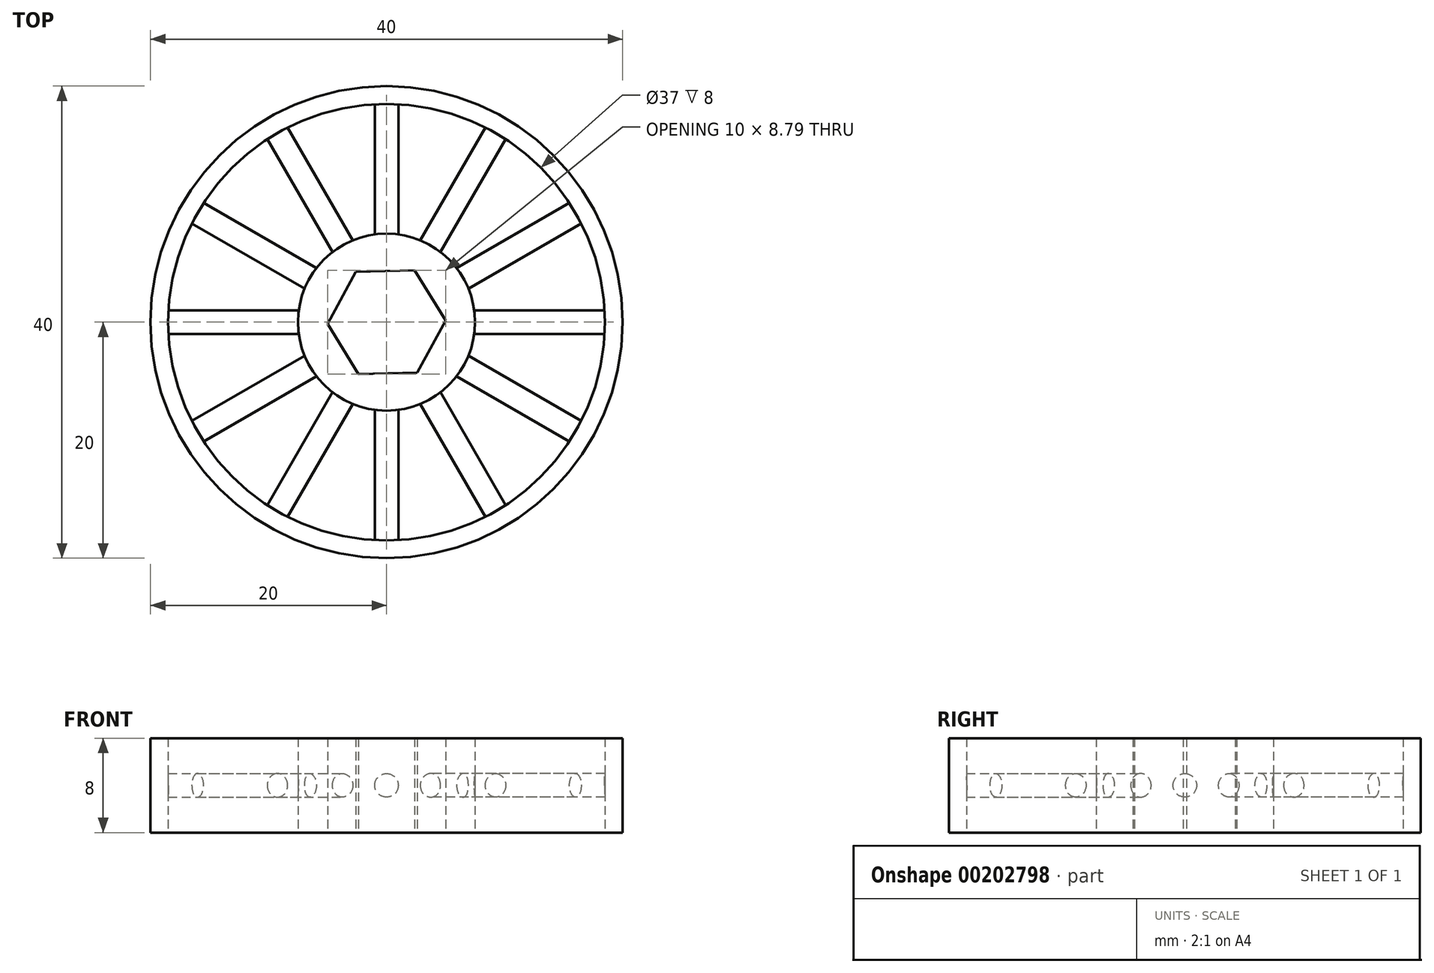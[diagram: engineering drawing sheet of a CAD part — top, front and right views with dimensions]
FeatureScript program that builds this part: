
annotation { "Feature Type Name" : "Feature", "Feature Type Description" : "" }
export const myFeature = defineFeature(function(context is Context, id is Id, definition is map)
    precondition{}
    {
        {
            var Q0;
            Q0=qCreatedBy(makeId("Top.planeOp"),FACE);
            var sketch = newSketch(context, id + "F0", { "sketchPlane" : qUnion([Q0])});
            skCircle(sketch, "E0", {"center": v(0, 0) * mm, "radius": 20 * mm});
            skCircle(sketch, "E1", {"center": v(0, 0) * mm, "radius": 5 * mm});
            skCircle(sketch, "E2", {"center": v(0, 0) * mm, "radius": 7.5 * mm});
            skCircle(sketch, "E3.cCircle", {"center": v(0, 0) * mm, "radius": 5 * mm, "construction": true});
            skLineSegment(sketch, "E3.0", {"start": v(2.61, -4.26) * mm, "end": v(-2.39, -4.4) * mm});
            skLineSegment(sketch, "E3.1", {"start": v(-2.39, -4.4) * mm, "end": v(-5, -0.13) * mm});
            skLineSegment(sketch, "E3.2", {"start": v(-5, -0.13) * mm, "end": v(-2.61, 4.26) * mm});
            skLineSegment(sketch, "E3.3", {"start": v(-2.61, 4.26) * mm, "end": v(2.39, 4.4) * mm});
            skLineSegment(sketch, "E3.4", {"start": v(2.39, 4.4) * mm, "end": v(5, 0.13) * mm});
            skLineSegment(sketch, "E3.5", {"start": v(5, 0.13) * mm, "end": v(2.61, -4.26) * mm});
            skCircle(sketch, "E4.0", {"center": v(0, 0) * mm, "radius": 18.5 * mm});
            skLineSegment(sketch, "E5.trimOffspring", {"start": v(7.5, 0) * mm, "end": v(18.5, 0) * mm, "construction": true});
            skLineSegment(sketch, "E6.0", {"start": v(7.43, -1) * mm, "end": v(18.47, -1) * mm});
            skLineSegment(sketch, "E7.0", {"start": v(7.43, 1) * mm, "end": v(18.47, 1) * mm});
            skSolve(sketch);
        }
        {
            var Q0;
            Q0=makeQuery(id+"F0.imprint","IMPRINT",FACE,{"disambiguationData":[TD([[makeQuery(id+"F0.imprint","IMPRINT",EDGE,{"derivedFrom":sQuery(id+"F0.wireOp",EDGE,"E0")}),1.0]])]});
            var Q1;
            Q1=makeQuery(id+"F0.imprint","IMPRINT",FACE,{"disambiguationData":[TD([[makeQuery(id+"F0.imprint","IMPRINT",EDGE,{"derivedFrom":sQuery(id+"F0.wireOp",EDGE,"E2")}),1.0]])]});
            var Q2;
            {var subQ0=sQuery(id+"F0.wireOp",EDGE,"E3.1");Q2=makeQuery(id+"F0.imprint","IMPRINT",FACE,{"disambiguationData":[TD([[makeQuery(id+"F0.imprint","IMPRINT",EDGE,{"derivedFrom":subQ0}),1.0]])]});}
            var Q3;
            {var subQ0=sQuery(id+"F0.wireOp",EDGE,"E3.2");Q3=makeQuery(id+"F0.imprint","IMPRINT",FACE,{"disambiguationData":[TD([[makeQuery(id+"F0.imprint","IMPRINT",EDGE,{"derivedFrom":subQ0}),1.0]])]});}
            var Q4;
            {var subQ0=sQuery(id+"F0.wireOp",EDGE,"E3.3");Q4=makeQuery(id+"F0.imprint","IMPRINT",FACE,{"disambiguationData":[TD([[makeQuery(id+"F0.imprint","IMPRINT",EDGE,{"derivedFrom":subQ0}),1.0]])]});}
            var Q5;
            {var subQ0=sQuery(id+"F0.wireOp",EDGE,"E3.4");Q5=makeQuery(id+"F0.imprint","IMPRINT",FACE,{"disambiguationData":[TD([[makeQuery(id+"F0.imprint","IMPRINT",EDGE,{"derivedFrom":subQ0}),1.0]])]});}
            var Q6;
            {var subQ0=sQuery(id+"F0.wireOp",EDGE,"E3.5");Q6=makeQuery(id+"F0.imprint","IMPRINT",FACE,{"disambiguationData":[TD([[makeQuery(id+"F0.imprint","IMPRINT",EDGE,{"derivedFrom":subQ0}),1.0]])]});}
            var Q7;
            {var subQ0=sQuery(id+"F0.wireOp",EDGE,"E3.0");Q7=makeQuery(id+"F0.imprint","IMPRINT",FACE,{"disambiguationData":[TD([[makeQuery(id+"F0.imprint","IMPRINT",EDGE,{"derivedFrom":subQ0}),1.0]])]});}
            extrude(context, id + "F1", {"entities" : qUnion([Q0, Q1, Q2, Q3, Q4, Q5, Q6, Q7]), "depth" : 4 * mm, "hasSecondDirection" : true, "secondDirectionOppositeDirection" : true, "secondDirectionDepth" : 4 * mm});
        }
        {
            var Q0;
            {var subQ0=sQuery(id+"F0.wireOp",EDGE,"E6.0");Q0=makeQuery(id+"F0.imprint","IMPRINT",FACE,{"disambiguationData":[TD([[makeQuery(id+"F0.imprint","IMPRINT",EDGE,{"derivedFrom":subQ0}),1.0]])]});}
            extrude(context, id + "F2", {"entities" : qUnion([Q0]), "depth" : 1 * mm, "hasSecondDirection" : true, "secondDirectionOppositeDirection" : true, "secondDirectionDepth" : 1 * mm});
        }
        {
            var Q0;
            Q0=qCreatedBy(makeId("Right.planeOp"),FACE);
            var sketch = newSketch(context, id + "F3", { "sketchPlane" : qUnion([Q0])});
            skLineSegment(sketch, "E8", {"start": v(0, -29.36) * mm, "end": v(0, 29.36) * mm, "construction": true});
            skSolve(sketch);
        }
        {
            var Q0;
            Q0=makeQuery(id+"F2.opExtrude","CAP_EDGE",EDGE,{"disambiguationData":[OSD([sQuery(id+"F0.wireOp",EDGE,"E6.0")])],"isStart":false});
            var Q1;
            Q1=makeQuery(id+"F2.opExtrude","CAP_EDGE",EDGE,{"disambiguationData":[OSD([sQuery(id+"F0.wireOp",EDGE,"E7.0")])],"isStart":false});
            var Q2;
            Q2=makeQuery(id+"F2.opExtrude","CAP_EDGE",EDGE,{"disambiguationData":[OSD([sQuery(id+"F0.wireOp",EDGE,"E6.0")])],"isStart":true});
            var Q3;
            Q3=makeQuery(id+"F2.opExtrude","CAP_EDGE",EDGE,{"disambiguationData":[OSD([sQuery(id+"F0.wireOp",EDGE,"E7.0")])],"isStart":true});
            fillet(context, id + "F4", {"entities" : qUnion([Q0, Q1, Q2, Q3]), "radius" : 1 * mm, "tangentPropagation" : true, "allowEdgeOverflow" : false});
        }
        {
            var Q0;
            Q0=makeQuery(id+"F2.opExtrude","SWEPT_BODY",BODY,{"disambiguationData":[OSD([sQuery(id+"F0.wireOp",EDGE,"E2"),sQuery(id+"F0.wireOp",EDGE,"E4.0"),sQuery(id+"F0.wireOp",EDGE,"E6.0"),sQuery(id+"F0.wireOp",EDGE,"E7.0")])]});
            var Q1;
            Q1=sQuery(id+"F3.wireOp",EDGE,"E8");
            circularPattern(context, id + "F5", {"entities" : qUnion([Q0]), "axis" : qUnion([Q1]), "angle" : 360 * degree, "instanceCount" : 12, "equalSpace" : true});
        }
    });
